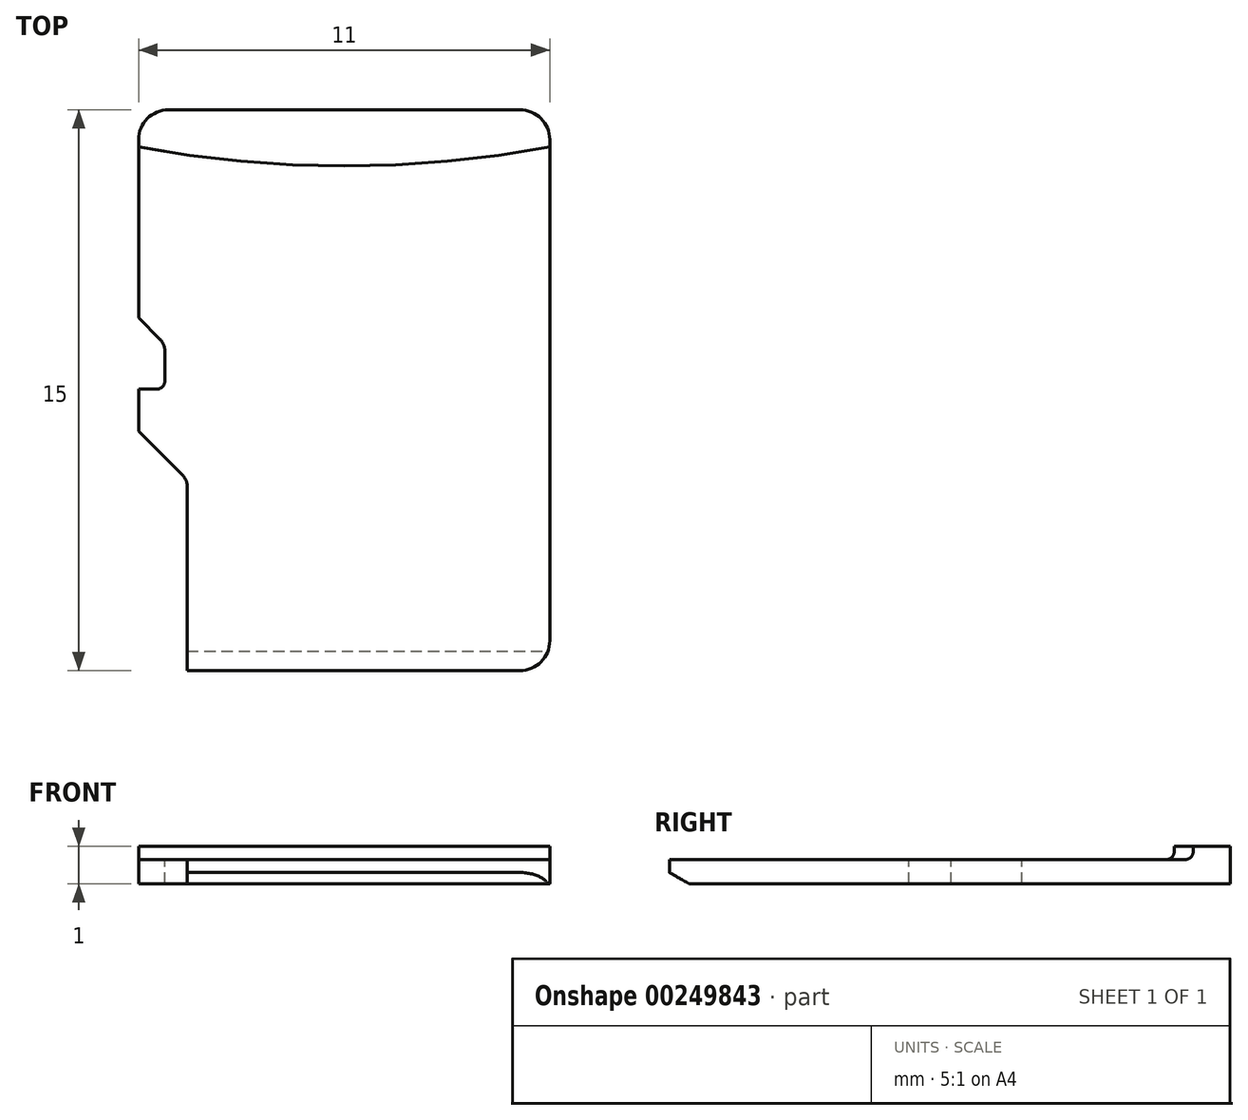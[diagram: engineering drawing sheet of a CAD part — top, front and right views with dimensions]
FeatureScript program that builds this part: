
annotation { "Feature Type Name" : "Feature", "Feature Type Description" : "" }
export const myFeature = defineFeature(function(context is Context, id is Id, definition is map)
    precondition{}
    {
        {
            var Q0;
            Q0=qCreatedBy(makeId("Top.planeOp"),FACE);
            var sketch = newSketch(context, id + "F0", { "sketchPlane" : qUnion([Q0])});
            skLineSegment(sketch, "E0.bottom", {"start": v(0, 0) * mm, "end": v(11, 0) * mm});
            skLineSegment(sketch, "E0.top", {"start": v(0, 15) * mm, "end": v(11, 15) * mm});
            skLineSegment(sketch, "E0.left", {"start": v(0, 0) * mm, "end": v(0, 15) * mm});
            skLineSegment(sketch, "E0.right", {"start": v(11, 0) * mm, "end": v(11, 15) * mm});
            skSolve(sketch);
        }
        {
            var Q0;
            Q0 = qSketchRegion(id + "F0", true);
            extrude(context, id + "F1", {"entities" : qUnion([Q0]), "depth" : 1 * mm});
        }
        {
            var Q0;
            Q0=makeQuery(id+"F1.opExtrude","CAP_FACE",FACE,{"disambiguationData":[OSD([sQuery(id+"F0.wireOp",EDGE,"E0.bottom"),sQuery(id+"F0.wireOp",EDGE,"E0.top"),sQuery(id+"F0.wireOp",EDGE,"E0.left"),sQuery(id+"F0.wireOp",EDGE,"E0.right")])],"isStart":false});
            var sketch = newSketch(context, id + "F2", { "sketchPlane" : qUnion([Q0])});
            skLineSegment(sketch, "E1", {"start": v(0, 0) * mm, "end": v(11, 0) * mm});
            skLineSegment(sketch, "E2", {"start": v(11, 0) * mm, "end": v(11, 14) * mm});
            skLineSegment(sketch, "E3", {"start": v(0, 0) * mm, "end": v(0, 14) * mm});
            skArc(sketch, "E4", {"start": v(0, 14) * mm, "mid": v(5.5, 13.5) * mm, "end": v(11, 14) * mm});
            skSolve(sketch);
        }
        {
            var Q0;
            Q0 = qSketchRegion(id + "F2", true);
            extrude(context, id + "F3", {"entities" : qUnion([Q0]), "operationType" : NewBodyOperationType.REMOVE, "oppositeDirection" : true, "depth" : 0.35 * mm});
        }
        {
            var Q0;
            Q0=makeQuery(id+"F3.boolean.opBoolean","COPY",FACE,{"derivedFrom":makeQuery(id+"F3.opExtrude","CAP_FACE",FACE,{"disambiguationData":[OSD([sQuery(id+"F2.wireOp",EDGE,"E1"),sQuery(id+"F2.wireOp",EDGE,"E2"),sQuery(id+"F2.wireOp",EDGE,"E3"),sQuery(id+"F2.wireOp",EDGE,"E4")])],"isStart":false})});
            var sketch = newSketch(context, id + "F4", { "sketchPlane" : qUnion([Q0])});
            skLineSegment(sketch, "E5", {"start": v(1.3, 0) * mm, "end": v(1.3, 5.1) * mm});
            skLineSegment(sketch, "E6", {"start": v(1.3, 5.1) * mm, "end": v(0, 6.4) * mm});
            skLineSegment(sketch, "E7", {"start": v(0, 6.4) * mm, "end": v(0, 7.53) * mm});
            skLineSegment(sketch, "E8", {"start": v(0, 7.53) * mm, "end": v(0.7, 7.53) * mm});
            skLineSegment(sketch, "E9", {"start": v(0.7, 7.53) * mm, "end": v(0.7, 8.73) * mm});
            skLineSegment(sketch, "E10", {"start": v(0.7, 8.73) * mm, "end": v(0, 9.43) * mm});
            skLineSegment(sketch, "E11", {"start": v(1.3, 0) * mm, "end": v(0, 0) * mm});
            skLineSegment(sketch, "E12", {"start": v(0, 0) * mm, "end": v(0, 6.4) * mm});
            skLineSegment(sketch, "E13", {"start": v(0, 7.53) * mm, "end": v(0, 9.43) * mm});
            skSolve(sketch);
        }
        {
            var Q0;
            Q0 = qSketchRegion(id + "F4", true);
            extrude(context, id + "F5", {"entities" : qUnion([Q0]), "operationType" : NewBodyOperationType.REMOVE, "endBound" : BoundingType.UP_TO_NEXT, "oppositeDirection" : true, "depth" : 25 * mm});
        }
        {
            var Q0;
            Q0=makeQuery(id+"F5.boolean.opBoolean","COPY",EDGE,{"derivedFrom":makeQuery(id+"F5.opExtrude","SWEPT_EDGE",EDGE,{"disambiguationData":[OSD([sQuery(id+"F4.wireOp",EDGE,"E8"),sQuery(id+"F4.wireOp",EDGE,"E9")])]})});
            fillet(context, id + "F6", {"entities" : qUnion([Q0]), "radius" : 0.2 * mm, "tangentPropagation" : true, "allowEdgeOverflow" : false});
        }
        {
            var Q0;
            Q0=makeQuery(id+"F5.boolean.opBoolean","COPY",EDGE,{"derivedFrom":makeQuery(id+"F5.opExtrude","SWEPT_EDGE",EDGE,{"disambiguationData":[OSD([sQuery(id+"F4.wireOp",EDGE,"E9"),sQuery(id+"F4.wireOp",EDGE,"E10")])]})});
            fillet(context, id + "F7", {"entities" : qUnion([Q0]), "radius" : 0.4 * mm, "tangentPropagation" : true, "allowEdgeOverflow" : false});
        }
        {
            var Q0;
            Q0=makeQuery(id+"F3.boolean.opBoolean","COPY",EDGE,{"derivedFrom":makeQuery(id+"F3.opExtrude","CAP_EDGE",EDGE,{"disambiguationData":[OSD([sQuery(id+"F2.wireOp",EDGE,"E4")])],"isStart":false})});
            fillet(context, id + "F8", {"entities" : qUnion([Q0]), "radius" : 0.2 * mm, "tangentPropagation" : true, "allowEdgeOverflow" : false});
        }
        {
            var Q0;
            Q0=makeQuery(id+"F5.boolean.opBoolean","COPY",EDGE,{"derivedFrom":makeQuery(id+"F5.opExtrude","SWEPT_EDGE",EDGE,{"disambiguationData":[OSD([sQuery(id+"F4.wireOp",EDGE,"E5"),sQuery(id+"F4.wireOp",EDGE,"E6")])]})});
            fillet(context, id + "F9", {"entities" : qUnion([Q0]), "radius" : 0.4 * mm, "tangentPropagation" : true, "allowEdgeOverflow" : false});
        }
        {
            var Q0;
            Q0=makeQuery(id+"F1.opExtrude","SWEPT_FACE",FACE,{"disambiguationData":[OSD([sQuery(id+"F0.wireOp",EDGE,"E0.right")])]});
            var sketch = newSketch(context, id + "F10", { "sketchPlane" : qUnion([Q0])});
            skLineSegment(sketch, "E14", {"start": v(0, 0.3) * mm, "end": v(0.52, 0) * mm});
            skLineSegment(sketch, "E15", {"start": v(0, 0.3) * mm, "end": v(0, 0) * mm});
            skLineSegment(sketch, "E16", {"start": v(0, 0) * mm, "end": v(0.52, 0) * mm});
            skSolve(sketch);
        }
        {
            var Q0;
            Q0 = qSketchRegion(id + "F10", true);
            extrude(context, id + "F11", {"entities" : qUnion([Q0]), "operationType" : NewBodyOperationType.REMOVE, "endBound" : BoundingType.UP_TO_NEXT, "oppositeDirection" : true, "depth" : 25 * mm});
        }
        {
            var Q0;
            Q0=makeQuery(id+"F1.opExtrude","SWEPT_EDGE",EDGE,{"disambiguationData":[OSD([sQuery(id+"F0.wireOp",EDGE,"E0.bottom"),sQuery(id+"F0.wireOp",EDGE,"E0.right")])]});
            var Q1;
            Q1=makeQuery(id+"F5.boolean.opBoolean","COPY",EDGE,{"derivedFrom":makeQuery(id+"F5.opExtrude","SWEPT_EDGE",EDGE,{"disambiguationData":[OSD([sQuery(id+"F2.wireOp",EDGE,"E1"),sQuery(id+"F4.wireOp",EDGE,"E5"),sQuery(id+"F4.wireOp",EDGE,"E11")])]})});
            var Q2;
            Q2=makeQuery(id+"F1.opExtrude","SWEPT_EDGE",EDGE,{"disambiguationData":[OSD([sQuery(id+"F0.wireOp",EDGE,"E0.top"),sQuery(id+"F0.wireOp",EDGE,"E0.left")])]});
            var Q3;
            Q3=makeQuery(id+"F1.opExtrude","SWEPT_EDGE",EDGE,{"disambiguationData":[OSD([sQuery(id+"F0.wireOp",EDGE,"E0.top"),sQuery(id+"F0.wireOp",EDGE,"E0.right")])]});
            fillet(context, id + "F12", {"entities" : qUnion([Q0, Q1, Q2, Q3]), "radius" : 0.8 * mm, "tangentPropagation" : true, "allowEdgeOverflow" : false});
        }
    });
